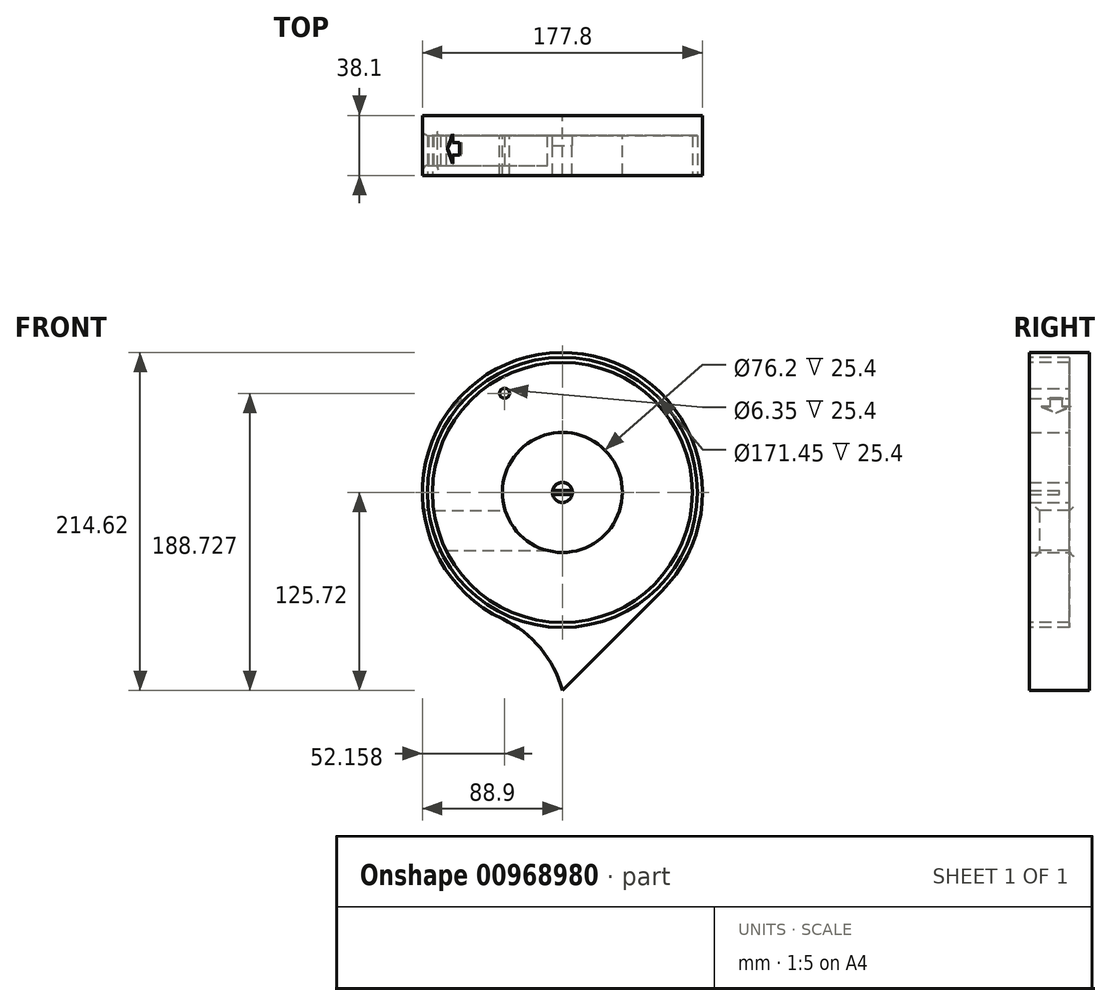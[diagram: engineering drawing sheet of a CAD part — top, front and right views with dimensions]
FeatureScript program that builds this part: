
annotation { "Feature Type Name" : "Feature", "Feature Type Description" : "" }
export const myFeature = defineFeature(function(context is Context, id is Id, definition is map)
    precondition{}
    {
        {
            var Q0;
            Q0=qCreatedBy(makeId("Front.planeOp"),FACE);
            var sketch = newSketch(context, id + "F0", { "sketchPlane" : qUnion([Q0])});
            skCircle(sketch, "E0", {"center": v(0, 0) * mm, "radius": 88.9 * mm});
            skSolve(sketch);
        }
        {
            var Q0;
            Q0 = qSketchRegion(id + "F0", true);
            extrude(context, id + "F1", {"entities" : qUnion([Q0]), "depth" : 12.7 * mm, "offsetDistance" : 25.4 * mm});
        }
        {
            var Q0;
            Q0=makeQuery(id+"F1.opExtrude","CAP_FACE",FACE,{"disambiguationData":[OSD([sQuery(id+"F0.wireOp",EDGE,"E0")])],"isStart":false});
            var sketch = newSketch(context, id + "F2", { "sketchPlane" : qUnion([Q0])});
            skCircle(sketch, "E1", {"center": v(0, 0) * mm, "radius": 82.55 * mm});
            skCircle(sketch, "E2", {"center": v(0, 0) * mm, "radius": 6.35 * mm});
            skSolve(sketch);
        }
        {
            var Q0;
            Q0=makeQuery(id+"F2.imprint","IMPRINT",FACE,{"disambiguationData":[TD([[makeQuery(id+"F2.imprint","IMPRINT",EDGE,{"derivedFrom":sQuery(id+"F2.wireOp",EDGE,"E1")}),-1.0]])]});
            var Q1;
            Q1=makeQuery(id+"F2.imprint","IMPRINT",FACE,{"disambiguationData":[TD([[makeQuery(id+"F2.imprint","IMPRINT",EDGE,{"derivedFrom":sQuery(id+"F2.wireOp",EDGE,"E2")}),1.0]])]});
            extrude(context, id + "F3", {"entities" : qUnion([Q0, Q1]), "operationType" : NewBodyOperationType.ADD, "depth" : 25.4 * mm, "offsetDistance" : 25.4 * mm});
        }
        {
            var Q0;
            Q0=makeQuery(id+"F3.opExtrude","CAP_FACE",FACE,{"disambiguationData":[OSD([sQuery(id+"F0.wireOp",EDGE,"E0"),sQuery(id+"F2.wireOp",EDGE,"E1")])],"isStart":false});
            var sketch = newSketch(context, id + "F4", { "sketchPlane" : qUnion([Q0])});
            skCircle(sketch, "E3.0", {"center": v(0, 0) * mm, "radius": 6.35 * mm});
            skArc(sketch, "E4", {"start": v(-38.97, 79.9) * mm, "mid": v(-51.1, 72.74) * mm, "end": v(-61.95, 63.76) * mm});
            skArc(sketch, "E5", {"start": v(-34.93, 74.8) * mm, "mid": v(-47.23, 67.7) * mm, "end": v(-58.14, 58.6) * mm});
            skLineSegment(sketch, "E6", {"start": v(-61.95, 63.76) * mm, "end": v(-58.14, 58.6) * mm});
            skLineSegment(sketch, "E7", {"start": v(-38.97, 79.9) * mm, "end": v(-34.93, 74.8) * mm});
            skSolve(sketch);
        }
        {
            var Q0;
            Q0=makeQuery(id+"F4.imprint","IMPRINT",FACE,{"disambiguationData":[TD([[makeQuery(id+"F4.imprint","IMPRINT",EDGE,{"derivedFrom":sQuery(id+"F4.wireOp",EDGE,"E4")}),1.0]])]});
            extrude(context, id + "F5", {"entities" : qUnion([Q0]), "operationType" : NewBodyOperationType.REMOVE, "oppositeDirection" : true, "depth" : 25.4 * mm, "offsetDistance" : 25.4 * mm});
        }
        {
            var Q0;
            Q0=makeQuery(id+"F5.boolean.opBoolean","MERGE",FACE,{"derivedFrom":[makeQuery(id+"F1.opExtrude","CAP_FACE",FACE,{"disambiguationData":[OSD([sQuery(id+"F0.wireOp",EDGE,"E0")])],"isStart":false})],"fromTools":[makeQuery(id+"F5.opExtrude","CAP_FACE",FACE,{"disambiguationData":[OSD([sQuery(id+"F4.wireOp",EDGE,"E4"),sQuery(id+"F4.wireOp",EDGE,"E5"),sQuery(id+"F4.wireOp",EDGE,"E6"),sQuery(id+"F4.wireOp",EDGE,"E7")])],"isStart":false})]});
            var sketch = newSketch(context, id + "F6", { "sketchPlane" : qUnion([Q0])});
            skLineSegment(sketch, "E8", {"start": v(0, 0) * mm, "end": v(-51.1, 72.74) * mm});
            skCircle(sketch, "E9", {"center": v(0, 0) * mm, "radius": 38.1 * mm});
            skLineSegment(sketch, "E10", {"start": v(0, 38.1) * mm, "end": v(0, 45.72) * mm});
            skLineSegment(sketch, "E11", {"start": v(0, 38.1) * mm, "end": v(-51.1, 72.74) * mm});
            skCircle(sketch, "E12", {"center": v(-36.74, 63) * mm, "radius": 3.18 * mm});
            skSolve(sketch);
        }
        {
            var Q0;
            {var subQ0=sQuery(id+"F6.wireOp",EDGE,"E12");var subQ1=sQuery(id+"F6.wireOp",EDGE,"E11");var subQ2=makeQuery(id+"F6.imprint","INTERSECT",VERTEX,{"disambiguationData":[OD(0.0)],"derivedFrom":[subQ1,subQ0]});Q0=makeQuery(id+"F6.imprint","IMPRINT",FACE,{"disambiguationData":[TD([[makeQuery(id+"F6.imprint","IMPRINT",EDGE,{"disambiguationData":[TD([[subQ2,-1.0]])],"derivedFrom":subQ1}),-1.0]])]});}
            var Q1;
            {var subQ0=sQuery(id+"F6.wireOp",EDGE,"E12");var subQ1=sQuery(id+"F6.wireOp",EDGE,"E11");var subQ2=makeQuery(id+"F6.imprint","INTERSECT",VERTEX,{"disambiguationData":[OD(0.0)],"derivedFrom":[subQ1,subQ0]});Q1=makeQuery(id+"F6.imprint","IMPRINT",FACE,{"disambiguationData":[TD([[makeQuery(id+"F6.imprint","IMPRINT",EDGE,{"disambiguationData":[TD([[subQ2,-1.0]])],"derivedFrom":subQ1}),1.0]])]});}
            extrude(context, id + "F7", {"entities" : qUnion([Q0, Q1]), "operationType" : NewBodyOperationType.ADD, "depth" : 25.4 * mm, "offsetDistance" : 25.4 * mm});
        }
        {
            var Q0;
            Q0=makeQuery(id+"F3.opExtrude","CAP_FACE",FACE,{"disambiguationData":[OSD([sQuery(id+"F2.wireOp",EDGE,"E2")])],"isStart":false});
            var sketch = newSketch(context, id + "F8", { "sketchPlane" : qUnion([Q0])});
            skLineSegment(sketch, "E13", {"start": v(-6.35, 0) * mm, "end": v(6.35, 0) * mm});
            skLineSegment(sketch, "E14", {"start": v(-6.35, 0) * mm, "end": v(-6.35, 1.27) * mm});
            skLineSegment(sketch, "E15", {"start": v(-6.35, 1.27) * mm, "end": v(6.35, 1.27) * mm});
            skLineSegment(sketch, "E16", {"start": v(6.35, 1.27) * mm, "end": v(6.35, 0) * mm});
            skLineSegment(sketch, "E17.MirrorCS", {"start": v(-6.35, 0) * mm, "end": v(-6.35, -1.27) * mm});
            skLineSegment(sketch, "E18.MirrorCS", {"start": v(-6.35, -1.27) * mm, "end": v(6.35, -1.27) * mm});
            skLineSegment(sketch, "E19.MirrorCS", {"start": v(6.35, -1.27) * mm, "end": v(6.35, 0) * mm});
            skSolve(sketch);
        }
        {
            var Q0;
            Q0 = qSketchRegion(id + "F8", true);
            extrude(context, id + "F9", {"entities" : qUnion([Q0]), "operationType" : NewBodyOperationType.REMOVE, "oppositeDirection" : true, "depth" : 19.05 * mm, "offsetDistance" : 25.4 * mm});
        }
        {
            var Q0;
            Q0=qCreatedBy(makeId("Right.planeOp"),FACE);
            var sketch = newSketch(context, id + "F10", { "sketchPlane" : qUnion([Q0])});
            skLineSegment(sketch, "E20.0", {"start": v(-38.1, -88.9) * mm, "end": v(-38.1, 88.9) * mm});
            skLineSegment(sketch, "E21.0", {"start": v(0, -88.9) * mm, "end": v(0, 88.9) * mm});
            skLineSegment(sketch, "E22.bottom", {"start": v(-31.75, -11.46) * mm, "end": v(-12.7, -11.46) * mm});
            skLineSegment(sketch, "E22.top", {"start": v(-31.75, -36.86) * mm, "end": v(-12.7, -36.86) * mm});
            skLineSegment(sketch, "E22.left", {"start": v(-31.75, -11.46) * mm, "end": v(-31.75, -36.86) * mm});
            skLineSegment(sketch, "E22.right", {"start": v(-12.7, -11.46) * mm, "end": v(-12.7, -36.86) * mm});
            skSolve(sketch);
        }
        {
            var Q0;
            Q0=makeQuery(id+"F10.imprint","IMPRINT",FACE,{"disambiguationData":[TD([[makeQuery(id+"F10.imprint","IMPRINT",EDGE,{"derivedFrom":sQuery(id+"F10.wireOp",EDGE,"E22.bottom")}),-1.0]])]});
            extrude(context, id + "F11", {"entities" : qUnion([Q0]), "operationType" : NewBodyOperationType.REMOVE, "endBound" : BoundingType.THROUGH_ALL, "oppositeDirection" : true, "depth" : 25.4 * mm, "offsetDistance" : 25.4 * mm});
        }
        {
            var Q0;
            {var subQ0=sQuery(id+"F0.wireOp",EDGE,"E0");Q0=makeQuery(id+"F11.boolean.opBoolean","INTERSECT",EDGE,{"derivedFrom":[makeQuery(id+"F3.boolean.opBoolean","MERGE",FACE,{"derivedFrom":[makeQuery(id+"F1.opExtrude","SWEPT_FACE",FACE,{"disambiguationData":[OSD([subQ0])]}),makeQuery(id+"F3.opExtrude","SWEPT_FACE",FACE,{"disambiguationData":[OSD([subQ0])]})]}),makeQuery(id+"F11.opExtrude","SWEPT_FACE",FACE,{"disambiguationData":[OSD([sQuery(id+"F10.wireOp",EDGE,"E22.bottom")])]})]});}
            var Q1;
            {var subQ0=sQuery(id+"F0.wireOp",EDGE,"E0");Q1=makeQuery(id+"F11.boolean.opBoolean","INTERSECT",EDGE,{"derivedFrom":[makeQuery(id+"F3.boolean.opBoolean","MERGE",FACE,{"derivedFrom":[makeQuery(id+"F1.opExtrude","SWEPT_FACE",FACE,{"disambiguationData":[OSD([subQ0])]}),makeQuery(id+"F3.opExtrude","SWEPT_FACE",FACE,{"disambiguationData":[OSD([subQ0])]})]}),makeQuery(id+"F11.opExtrude","SWEPT_FACE",FACE,{"disambiguationData":[OSD([sQuery(id+"F10.wireOp",EDGE,"E22.right")])]})]});}
            var Q2;
            {var subQ0=sQuery(id+"F0.wireOp",EDGE,"E0");Q2=makeQuery(id+"F11.boolean.opBoolean","INTERSECT",EDGE,{"derivedFrom":[makeQuery(id+"F3.boolean.opBoolean","MERGE",FACE,{"derivedFrom":[makeQuery(id+"F1.opExtrude","SWEPT_FACE",FACE,{"disambiguationData":[OSD([subQ0])]}),makeQuery(id+"F3.opExtrude","SWEPT_FACE",FACE,{"disambiguationData":[OSD([subQ0])]})]}),makeQuery(id+"F11.opExtrude","SWEPT_FACE",FACE,{"disambiguationData":[OSD([sQuery(id+"F10.wireOp",EDGE,"E22.top")])]})]});}
            var Q3;
            {var subQ0=sQuery(id+"F0.wireOp",EDGE,"E0");Q3=makeQuery(id+"F11.boolean.opBoolean","INTERSECT",EDGE,{"derivedFrom":[makeQuery(id+"F3.boolean.opBoolean","MERGE",FACE,{"derivedFrom":[makeQuery(id+"F1.opExtrude","SWEPT_FACE",FACE,{"disambiguationData":[OSD([subQ0])]}),makeQuery(id+"F3.opExtrude","SWEPT_FACE",FACE,{"disambiguationData":[OSD([subQ0])]})]}),makeQuery(id+"F11.opExtrude","SWEPT_FACE",FACE,{"disambiguationData":[OSD([sQuery(id+"F10.wireOp",EDGE,"E22.left")])]})]});}
            fillet(context, id + "F12", {"entities" : qUnion([Q0, Q1, Q2, Q3]), "radius" : 2.54 * mm, "tangentPropagation" : true, "allowEdgeOverflow" : false});
        }
        {
            var Q0;
            Q0=makeQuery(id+"F3.opExtrude","CAP_FACE",FACE,{"disambiguationData":[OSD([sQuery(id+"F0.wireOp",EDGE,"E0"),sQuery(id+"F2.wireOp",EDGE,"E1")])],"isStart":false});
            var sketch = newSketch(context, id + "F13", { "sketchPlane" : qUnion([Q0])});
            skCircle(sketch, "E23", {"center": v(0, 0) * mm, "radius": 82.55 * mm});
            skCircle(sketch, "E24", {"center": v(0, 0) * mm, "radius": 85.73 * mm});
            skSolve(sketch);
        }
        {
            var Q0;
            {var subQ0=sQuery(id+"F13.wireOp",EDGE,"E23");var subQ1=makeQuery(id+"F5.boolean.opBoolean","COPY",EDGE,{"derivedFrom":makeQuery(id+"F5.opExtrude","CAP_EDGE",EDGE,{"disambiguationData":[OSD([sQuery(id+"F4.wireOp",EDGE,"E7")])],"isStart":true})});var subQ2=makeQuery(id+"F13.imprint","INTERSECT",VERTEX,{"derivedFrom":[subQ1,subQ0]});Q0=makeQuery(id+"F13.imprint","IMPRINT",FACE,{"disambiguationData":[TD([[makeQuery(id+"F13.imprint","IMPRINT",EDGE,{"disambiguationData":[TD([[subQ2,1.0]])],"derivedFrom":subQ0}),-1.0]])]});}
            extrude(context, id + "F14", {"entities" : qUnion([Q0]), "operationType" : NewBodyOperationType.REMOVE, "oppositeDirection" : true, "depth" : 25.4 * mm, "offsetDistance" : 25.4 * mm});
        }
        {
            var Q0;
            Q0=makeQuery(id+"FJMDsK356Akih9Z_1.boolean.opBoolean","MERGE",FACE,{"derivedFrom":[makeQuery(id+"F1.opExtrude","CAP_FACE",FACE,{"disambiguationData":[OSD([sQuery(id+"F0.wireOp",EDGE,"E0")])],"isStart":true})],"fromTools":[makeQuery(id+"FJMDsK356Akih9Z_1.opExtrude","SWEPT_FACE",FACE,{"disambiguationData":[OSD([sQuery(id+"FCoRcMF40WGkSkM_1.wireOp",EDGE,"rMcAN4Fs-YPcF-QuV1-B9MU-nLGjg00mM8Cc")])]})]});
            var sketch = newSketch(context, id + "F15", { "sketchPlane" : qUnion([Q0])});
            skLineSegment(sketch, "E25", {"start": v(0, 0) * mm, "end": v(0, -88.9) * mm});
            skLineSegment(sketch, "E26", {"start": v(0, 0) * mm, "end": v(-62.86, -62.86) * mm});
            skLineSegment(sketch, "E27", {"start": v(-62.86, -62.86) * mm, "end": v(0, -125.72) * mm});
            skArc(sketch, "E28", {"start": v(37.85, -80.44) * mm, "mid": v(13.92, -98.9) * mm, "end": v(0, -125.72) * mm});
            skArc(sketch, "E29.MirrorCS", {"start": v(-80.44, 37.85) * mm, "mid": v(-98.9, 13.92) * mm, "end": v(-125.72, 0) * mm});
            skLineSegment(sketch, "E30.MirrorCS", {"start": v(-62.86, -62.86) * mm, "end": v(-125.72, 0) * mm});
            skSolve(sketch);
        }
        {
            var Q0;
            {var subQ0=sQuery(id+"F15.wireOp",EDGE,"E29.MirrorCS");Q0=makeQuery(id+"F15.imprint","IMPRINT",FACE,{"disambiguationData":[TD([[makeQuery(id+"F15.imprint","IMPRINT",EDGE,{"derivedFrom":subQ0}),1.0]])]});}
            var Q1;
            {var subQ0=sQuery(id+"F15.wireOp",EDGE,"E27");Q1=makeQuery(id+"F15.imprint","IMPRINT",FACE,{"disambiguationData":[TD([[makeQuery(id+"F15.imprint","IMPRINT",EDGE,{"derivedFrom":subQ0}),1.0]])]});}
            extrude(context, id + "F16", {"entities" : qUnion([Q0, Q1]), "operationType" : NewBodyOperationType.ADD, "oppositeDirection" : true, "depth" : 38.1 * mm, "offsetDistance" : 25.4 * mm});
        }
        {
            var Q0;
            Q0=qCreatedBy(makeId("Top.planeOp"),FACE);
            var Q1;
            Q1=qCreatedBy(makeId("Right.planeOp"),FACE);
            cPlane(context, id + "F17", {"entities" : qUnion([Q0, Q1]), "cplaneType" : CPlaneType.MID_PLANE, "offset" : 25.4 * mm, "width" : 152.4 * mm, "height" : 152.4 * mm});
        }
        {
            var Q0;
            Q0=qCreatedBy(id+"F17.planeOp",FACE);
            cPlane(context, id + "F18", {"entities" : qUnion([Q0]), "cplaneType" : CPlaneType.OFFSET, "offset" : 87.12 * mm, "width" : 152.4 * mm, "height" : 152.4 * mm});
        }
        {
            var Q0;
            Q0=qCreatedBy(id+"F18.planeOp",FACE);
            var sketch = newSketch(context, id + "F19", { "sketchPlane" : qUnion([Q0])});
            skLineSegment(sketch, "E31", {"start": v(17.16, -3.58) * mm, "end": v(25.16, -3.58) * mm});
            skLineSegment(sketch, "E32", {"start": v(25.16, -3.58) * mm, "end": v(25.16, -10.57) * mm});
            skLineSegment(sketch, "E33", {"start": v(25.16, -10.57) * mm, "end": v(30.46, -10.57) * mm});
            skLineSegment(sketch, "E34", {"start": v(30.46, -10.57) * mm, "end": v(21.16, -15.92) * mm});
            skPoint(sketch, "E34.endSnap0", {"position": v(21.16, -3.58) * mm});
            skLineSegment(sketch, "E35", {"start": v(21.16, -15.92) * mm, "end": v(11.97, -10.57) * mm});
            skLineSegment(sketch, "E36", {"start": v(11.97, -10.57) * mm, "end": v(17.16, -10.57) * mm});
            skLineSegment(sketch, "E37", {"start": v(17.16, -10.57) * mm, "end": v(17.16, -3.58) * mm});
            skSolve(sketch);
        }
        {
            var Q0;
            Q0 = qSketchRegion(id + "F19", true);
            extrude(context, id + "F20", {"entities" : qUnion([Q0]), "operationType" : NewBodyOperationType.REMOVE, "depth" : 25.4 * mm, "offsetDistance" : 25.4 * mm});
        }
    });
